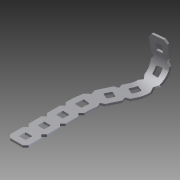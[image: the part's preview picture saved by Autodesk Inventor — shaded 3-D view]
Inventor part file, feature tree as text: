
AUTODESK INVENTOR PART (.ipt)
format: ipt  version: 2014 SP1 (Build 180222100, 222)  size: 902,656 bytes
history: native  units: in
note: dims shown in document units (in); Inventor stores cm internally (conversion verified against a paired STEP export)
features: other x4, sketch x4, imported_body x1, extrude x1
ambient origin geometry x8: Origin, YZ Plane, XZ Plane, XY Plane, X Axis, Y Axis, Z Axis, Center Point
bodies: Body1 (feature_tree)
feature tree (10):
  parser-record x1  (decoder bookkeeping rows leaked as tree rows — omitted from the tree; the rows remain in map.json)
  imported_body  "Base1"
  extrude  "Extrusion1"  Depth=1.0in TaperAngle=0.0deg
  other  "Bend Part1"
  other  "Bend Part2"
  other  "Bend Part3"
  sketch  "Sketch1"  dims[d0=4.0in d1=1.0in d2=0.0in]
  sketch  "Sketch2"  dims[d3=0.5in d4=0.6528in]
  sketch  "Sketch4"  dims[d5=0.1787in d6=0.5in]
  sketch  "Sketch5"  dims[d7=0.1787in d8=0.5in]
